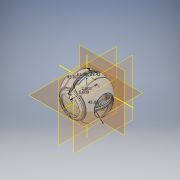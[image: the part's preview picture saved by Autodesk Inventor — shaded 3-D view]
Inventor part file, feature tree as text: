
AUTODESK INVENTOR PART (.ipt)
format: ipt  version: 2019 (Build 230136000, 136)  size: 1,138,688 bytes
history: native  units: in
note: dims shown in document units (in); Inventor stores cm internally (conversion verified against a paired STEP export)
features: sketch x14, mirror x10, plane x9, revolve x8, chamfer x8, extrude x7, fillet x5, projected_geometry x4, other x3
ambient origin geometry x8: Origin, YZ Plane, XZ Plane, XY Plane, X Axis, Y Axis, Z Axis, Center Point
bodies: Solid1 (feature_tree)
feature tree (68):
  other  "Wheatly.ipt"
  plane  "Work Plane1"
  revolve  "Revolution1"  [1 undecoded]
  mirror  "Mirror1"
  plane  "Work Plane2"
  extrude  "Extrusion1"  Depth=0.3966in
  revolve  "Revolution2"  [1 undecoded]
  fillet  "Fillet1"  Radius=0.375in
  fillet  "Fillet2"  Radius=0.25in
  fillet  "Fillet3"  Radius=3.1in
  fillet  "Fillet4"  Radius=0.4438in
  chamfer  "Chamfer1"  Distance=1.0in
  chamfer  "Chamfer2"  Distance=2.0752in
  chamfer  "Chamfer3"  Distance=0.075in
  chamfer  "Chamfer4"  Distance=0.025in
  chamfer  "Chamfer5"  Distance=0.13in
  chamfer  "Chamfer6"  Distance=0.13in
  chamfer  "Chamfer7"  Distance=0.13in
  chamfer  "Chamfer8"  Distance=0.13in
  plane  "Work Plane3"
  mirror  "Mirror2"
  plane  "Work Plane4"
  revolve  "Revolution3"  [1 undecoded]
  plane  "Work Plane5"
  mirror  "Mirror3"
  revolve  "Revolution4"  [1 undecoded]
  sketch  "Sketch16"  dims[d4=0.3966in d5=0.75in d6=0.375in d7=0.25in d8=3.1in d9=0.4438in]
  revolve  "Revolution5"  [1 undecoded]
  revolve  "Revolution6"  [1 undecoded]
  mirror  "Mirror4"
  sketch  "Sketch20"  dims[d11=2.8in d12=1.0in d13=0.0in]
  revolve  "Revolution8"  Angle=45.0deg
  mirror  "Mirror5"
  revolve  "Revolution9"  [1 undecoded]
  plane  "Work Plane6"
  extrude  "Extrusion2"  Depth=2.0752in
  fillet  "Fillet5"  Radius=2.875in
  mirror  "Mirror6"
  mirror  "Mirror7"
  plane  "Work Plane7"
  sketch  "Sketch24"  dims[d16=0.5in]
  extrude  "Extrusion3"  Depth=2.85in
  plane  "Work Plane8"
  extrude  "Extrusion4"  Depth=2.85in
  mirror  "Mirror8"
  mirror  "Mirror9"
  extrude  "Extrusion5"  Depth=6.1in
  extrude  "Extrusion6"  Depth=6.0in
  extrude  "Extrusion7"  TaperAngle=60.0deg  [1 undecoded]
  mirror  "Mirror10"
  sketch  "Sketch31"  dims[d22=0.1in d23=2.0752in d24=0.075in d25=0.025in d26=0.13in d27=0.1in d28=1.2025in d29=0.13in d30=0.1in d31=1.2025in d32=0.13in d33=0.1in d34=1.2025in d35=0.13in d36=0.1in d37=1.2025in d38=0.13in d39=0.1in d40=1.2025in d41=0.13in d42=0.1in d43=1.2025in d44=0.13in d45=0.1in d46=1.2025in d47=0.13in d48=0.1in d49=1.2025in d50=45.0deg d51=3.0in d52=2.0752in d53=2.875in d55=1.5in d62=2.85in d63=2.85in d64=6.1in d65=6.0in d66=60.0deg d67=2.0in d69=60.0deg d71=1.5in d72=60.0deg d75=2.8031in d76=0.1747in d77=6.0in d78=0.327in d79=0.327in d80=0.6871in d81=0.3172in d82=0.3172in d83=0.15in d84=3.0in d85=0.2in d88=0.075in d89=0.6871in d90=1.8in d91=2.75in d92=3.1in d93=0.1in d94=0.0in d95=-2.0in d96=3.3in d97=0.5in d98=0.0in d99=2.5in d100=1.25in d101=0.25in d102=0.0in d103=2.9in d104=0.25in d105=0.0in d106=0.2in d107=2.45in d108=0.6in d109=3.4375in d110=0.0in d111=0.25in d112=0.0in d113=6.0in d114=45.0deg]
  plane  "Work Plane9"
  other  "Solid1::Wheatly.ipt"
  other  "TaggingFeature1"
  sketch  "Sketch5"  dims[d0=0.3937in d1=2.5in]
  sketch  "Sketch10"  dims[d2=6.0in d3=0.3966in]
  projected_geometry  "Projected Loop1"
  projected_geometry  "Projected Loop2"
  projected_geometry  "Projected Loop3"
  sketch  "Sketch17"  dims[d10=-3.0in]
  projected_geometry  "Projected Loop4"
  sketch  "Sketch22"  dims[d14=0.4192in]
  sketch  "Sketch23"  dims[d15=5.7in]
  sketch  "Sketch25"  dims[d17=0.25in]
  sketch  "Sketch26"  dims[d18=0.15in]
  sketch  "Sketch27"  dims[d19=0.1in]
  sketch  "Sketch28"  dims[d20=0.1in]
  sketch  "Sketch29"  dims[d21=0.15in]
note: 8 required parameter values undecoded (feature->parameter linkage not recoverable at this tier; creation-order binding heuristic only, values carry confidence <= 0.55)